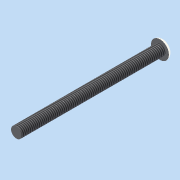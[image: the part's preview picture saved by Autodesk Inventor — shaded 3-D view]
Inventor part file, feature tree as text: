
AUTODESK INVENTOR PART (.ipt)
format: ipt  version: 2015 (Build 190159000, 159)  size: 90,624 bytes
history: native  units: mm
features: revolve x1, fillet x1, thread x1, sketch x1
ambient origin geometry x8: Origin, YZ Plane, XZ Plane, XY Plane, X Axis, Y Axis, Z Axis, Center Point
bodies: Solid1 (feature_tree)
feature tree (4):
  revolve  "Revolution1"  [1 undecoded]
  fillet  "Fillet1"  Radius=1.0mm
  thread  "Thread1"  [1 undecoded]
  sketch  "Sketch1"  dims[d0=1.5mm d1=2.5mm d2=1.0mm d3=90.0deg d4=1.0mm d5=10.0mm d6=0.0mm d7=40.0mm]
note: 2 required parameter values undecoded (feature->parameter linkage not recoverable at this tier; creation-order binding heuristic only, values carry confidence <= 0.55)